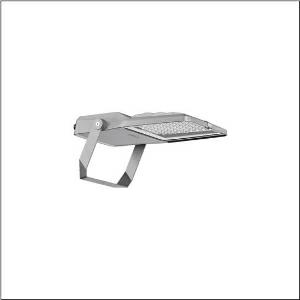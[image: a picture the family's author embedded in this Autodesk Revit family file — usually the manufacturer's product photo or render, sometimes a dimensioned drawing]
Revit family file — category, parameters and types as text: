
# Revit family: floodlight_fl_21_mini___pl52_5xa7776c4d1a_cdf3
name_source: partatom
category: Lighting Fixtures
units: mm (PartAtom-declared; Revit-internal decimal feet)

## family parameters
Cut with Voids When Loaded = No
Host = Face
Light Source = No
Part Type = Normal
Room Calculation Point = No
Round Connector Dimension = Use Diameter
Shared = No

## types (1)
- --- (1 x LED, 12700 lm, 89 W, 4000K)
    Apparent Load = 89 VA
    CIE Flux Codes = 26 60 98 100 100
    Color Rendering = 70
    Color Temperature = 4000K
    Default Elevation = 1800 mm
    Description = Floodlight FL 21 mini, floodlight, primary light control with lens, of PMMA, primary optical cover: protective disc, of toughened safety glass, transparent, light distribution: PL52, light emission: direct distribution, installation type: surface-mounted, LED, High Power LED, rated luminous flux: 12.700lm, luminous efficacy: 143lm/W, light colour: 740, colour temperature: 4000K, control gear: D4iSmart Interface (Zhaga), control: overheat protection, constant luminous flux control, time-dependent luminous flux control, flexible luminous flux parameterisation, pre-setting: logarithmic dimming characteristic, with terminal, 6-pole, mains connection: 220..240V, AC, 50/60Hz, start of lifetime: 89W, end of service life: 94W, reduction: 43W, mounting bracket, of diecast aluminium, powder-coated, SITECO metallic grey (DB 702S), corrosivity category C5 mid according to DIN EN ISO 12944, suitable for swimming pools, chlorine-resistant, sealing non-destructively replaceable, mounting bracket, of steel, galvanised, powder-coated, SITECO metallic grey (DB 702S), Smart Interface below and above, protection rating (complete): IP66, insulation class (complete): insulation class II (safety insulation), certification: CE, ENEC, VDE, protection symbol: D, impact resistance: IK08, permissible operating ambient temperature: -40..+40°C, permissible operating ambient temperature for outdoor applications: -40..+50°C, standard: DIN EN 12944, LABS conformity tested according to VDMA 24364:2018-05, packaging unit: 1 piece

Light Distribution: PL52
    Height = 70 mm
    Lamp = 1 x LED
    Lamp Light Flux = 12700 lm
    Lamp Power = 89 W
    Lamp count = 1
    Length = 485 mm
    Luminous efficacy = 143 lm/W
    Manufacturer = Siteco
    ModVariant = No
    Model = 5XA7776C4D1A
    Number of Poles = 1
    OnlyDefault = Yes
    Power Factor = 1
    Product Name = Floodlight FL 21 mini | PL52
    Product group = floodlight | pylon annexe
    ProductGroupID = 6201
    Protection Class = Protection class II
    Protection Degree = IP 66
    RLX_Detail_Level = 1
    RLX_Emergency_Light_Flux = 0 lm
    RLX_Emergency_Type = 0
    RLX_Emergency_Type_DB = No
    RlxData = <blob elided: 96453 chars, md5=d55490fd>
    Socket = socket
    Standby Power = 0 W
    System Light Flux = 12700 lm
    System Power = 89 W
    Type Comments = factory setting: luminous flux: 100 % | dim-lin: 254 | 456 mA
    Type Image = l_1006845.jpg
    URL = http://relux.com
    VarID = @adj_099337
    Voltage = 0 V
    Weight = 0.00 kg
    Width = 337 mm

## geometry (parser evidence)
native form markers: Blend x4, Sweep x14
no freeform markers — native parametric forms only
